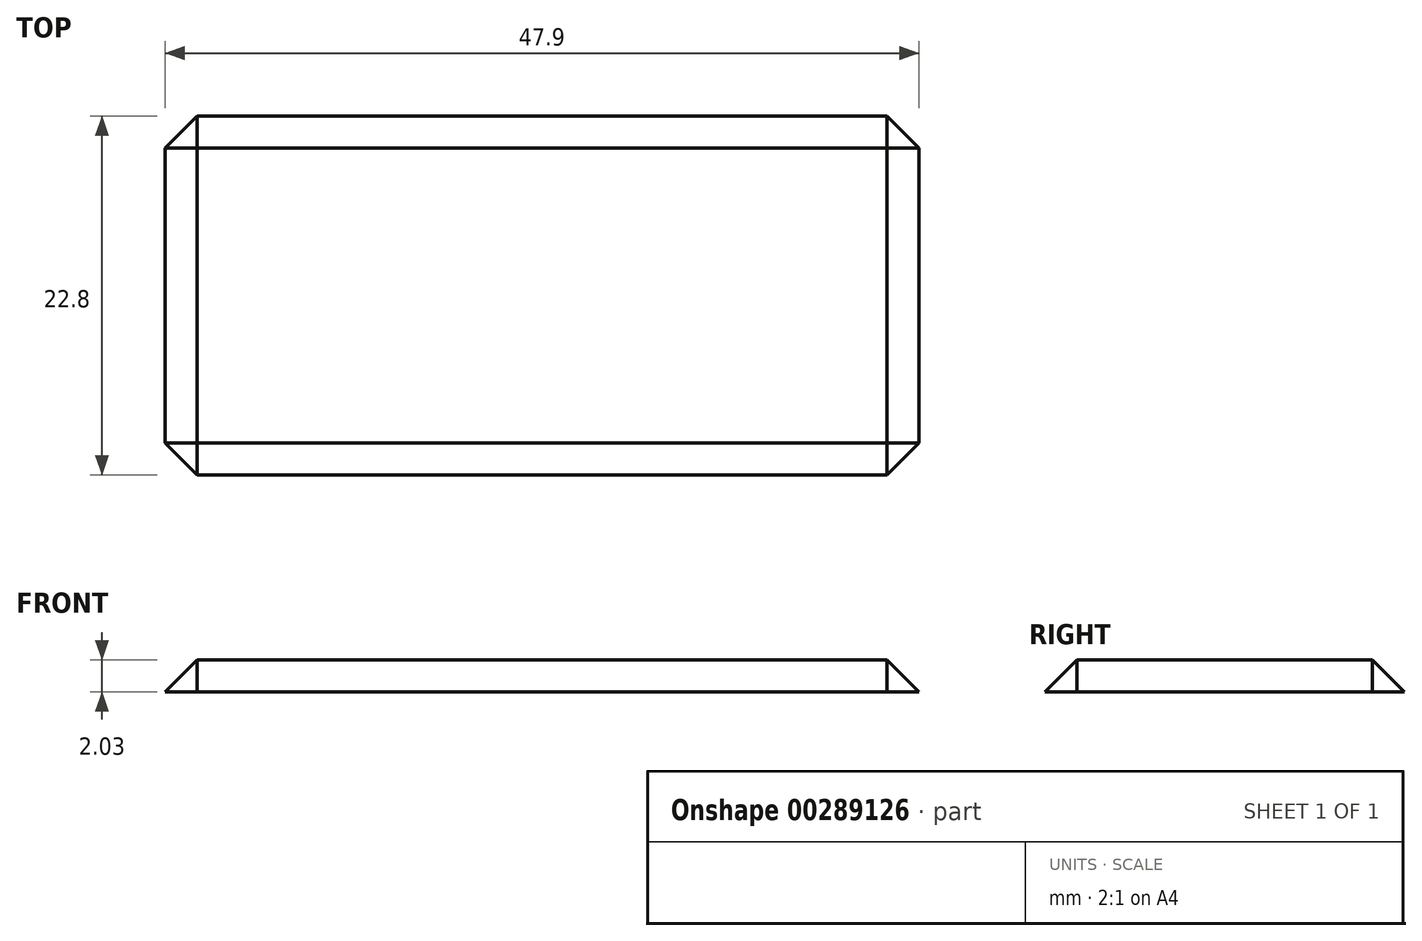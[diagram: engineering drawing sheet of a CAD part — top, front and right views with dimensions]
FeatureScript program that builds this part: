
annotation { "Feature Type Name" : "Feature", "Feature Type Description" : "" }
export const myFeature = defineFeature(function(context is Context, id is Id, definition is map)
    precondition{}
    {
        {
            var Q0;
            Q0=qCreatedBy(makeId("Top.planeOp"),FACE);
            var sketch = newSketch(context, id + "F0", { "sketchPlane" : qUnion([Q0])});
            skLineSegment(sketch, "E0.bottom", {"start": v(-23.95, 11.4) * mm, "end": v(23.95, 11.4) * mm});
            skLineSegment(sketch, "E0.top", {"start": v(-23.95, -11.4) * mm, "end": v(23.95, -11.4) * mm});
            skLineSegment(sketch, "E0.left", {"start": v(-23.95, 11.4) * mm, "end": v(-23.95, -11.4) * mm});
            skLineSegment(sketch, "E0.right", {"start": v(23.95, 11.4) * mm, "end": v(23.95, -11.4) * mm});
            skLineSegment(sketch, "E1", {"start": v(0, 0) * mm, "end": v(0, 11.4) * mm, "construction": true});
            skLineSegment(sketch, "E2", {"start": v(0, 0) * mm, "end": v(0, -11.4) * mm, "construction": true});
            skLineSegment(sketch, "E3", {"start": v(-23.95, 0) * mm, "end": v(0, 0) * mm, "construction": true});
            skLineSegment(sketch, "E4", {"start": v(0, 0) * mm, "end": v(23.95, 0) * mm, "construction": true});
            skSolve(sketch);
        }
        {
            var Q0;
            Q0=makeQuery(id+"F0.imprint","IMPRINT",FACE,{"disambiguationData":[TD([[makeQuery(id+"F0.imprint","IMPRINT",EDGE,{"derivedFrom":sQuery(id+"F0.wireOp",EDGE,"E0.bottom")}),-1.0]])]});
            extrude(context, id + "F1", {"entities" : qUnion([Q0]), "depth" : 2.03 * mm});
        }
        {
            var Q0;
            Q0=makeQuery(id+"F1.opExtrude","CAP_EDGE",EDGE,{"disambiguationData":[OSD([sQuery(id+"F0.wireOp",EDGE,"E0.top")])],"isStart":false});
            var Q1;
            Q1=makeQuery(id+"F1.opExtrude","CAP_EDGE",EDGE,{"disambiguationData":[OSD([sQuery(id+"F0.wireOp",EDGE,"E0.left")])],"isStart":false});
            var Q2;
            Q2=makeQuery(id+"F1.opExtrude","CAP_EDGE",EDGE,{"disambiguationData":[OSD([sQuery(id+"F0.wireOp",EDGE,"E0.bottom")])],"isStart":false});
            var Q3;
            Q3=makeQuery(id+"F1.opExtrude","CAP_EDGE",EDGE,{"disambiguationData":[OSD([sQuery(id+"F0.wireOp",EDGE,"E0.right")])],"isStart":false});
            var Q4;
            Q4=makeQuery(id+"F1.opExtrude","SWEPT_EDGE",EDGE,{"disambiguationData":[OSD([sQuery(id+"F0.wireOp",EDGE,"E0.top"),sQuery(id+"F0.wireOp",EDGE,"E0.right")])]});
            var Q5;
            Q5=makeQuery(id+"F1.opExtrude","SWEPT_EDGE",EDGE,{"disambiguationData":[OSD([sQuery(id+"F0.wireOp",EDGE,"E0.top"),sQuery(id+"F0.wireOp",EDGE,"E0.left")])]});
            var Q6;
            Q6=makeQuery(id+"F1.opExtrude","SWEPT_EDGE",EDGE,{"disambiguationData":[OSD([sQuery(id+"F0.wireOp",EDGE,"E0.bottom"),sQuery(id+"F0.wireOp",EDGE,"E0.right")])]});
            var Q7;
            Q7=makeQuery(id+"F1.opExtrude","SWEPT_EDGE",EDGE,{"disambiguationData":[OSD([sQuery(id+"F0.wireOp",EDGE,"E0.bottom"),sQuery(id+"F0.wireOp",EDGE,"E0.left")])]});
            chamfer(context, id + "F2", {"entities" : qUnion([Q0, Q1, Q2, Q3, Q4, Q5, Q6, Q7]), "width" : 2.03 * mm, "tangentPropagation" : true});
        }
    });
